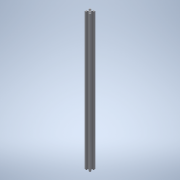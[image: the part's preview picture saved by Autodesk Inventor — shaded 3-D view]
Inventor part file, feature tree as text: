
AUTODESK INVENTOR PART (.ipt)
format: ipt  version: 2022.1 (Build 261234020, 234B)  size: 200,192 bytes
history: native  units: mm
features: extrude x1, sketch x1
ambient origin geometry x8: Origin, YZ Plane, XZ Plane, XY Plane, X Axis, Y Axis, Z Axis, Center Point
bodies: Body1 (feature_tree)
feature tree (2):
  extrude  "Extrusion9"  [1 undecoded]
  sketch  "Sketch1"  dims[d44=527.05mm d45=0.0mm]
note: 1 required parameter value undecoded (feature->parameter linkage not recoverable at this tier; creation-order binding heuristic only, values carry confidence <= 0.55)
